# Revit family: P300328-009
name_source: partatom
category: Lighting Fixtures
revit_build: Autodesk Revit 2017 (Build: 20160225_1515(x64)
units: mm (PartAtom-declared; Revit-internal decimal feet)

## family parameters
Cut with Voids When Loaded = No
Host = Face
Light Source = No
OmniClass Number = 23.80.70.11.14.17
OmniClass Title = Direct/Indirect
Part Type = Normal
Room Calculation Point = No
Round Connector Dimension = Use Diameter
Shared = Yes

## types (1)
- P300328-009
    Apparent Load = 100 VA
    Assembly Code = D5020200
    Connector Description = Lighting Connector
    Default Elevation = 48 "
    Description = Merry Collection Two-Light Brushed Nickel and Etched Glass Transitional Style Bath Vanity Wall Light
    Features = Bring a modern vibe to any room with the Merry Collection 2-Light Brushed Nickel Etched Glass Transitional Bath Vanity Light. The clean-lined frame, tubular arm, and round light base are coated in a silver brushed nickel finish. A light source glows from inside a crisp etched glass shade.
Application: Bring a modern vibe to any room with the Merry Collection 2-Light Brushed Nickel Etched Glass Transitional Bath Vanity Light ideal for any entryway, hallway, foyer, bedroom, sitting room, living room, or bathroom.
Styles: Perfect for transitional and contemporary style settings.
Finish: The clean-lined frame, tubular arm, and round light base are coated in silver brushed nickel finish.
Materials: Constructed from steel to ensure a long product lifespan. Mount the light fixture facing up or down.
Glass/Shade: Light sources glow from inside crisp etched glass shades.
Bulbs: For ideal illumination, use 2 medium base bulbs that are sold separately (100w max - LED/CFL/incandescent). Compatible with dimmable bulbs.
Dimensions: Measures 12-inch width by 8-1/4-inch height by 5-3/4-inch depth.
Certifications: cULus damp location listed.
Pairs With: Pairs with the Tobin, Etched Glass, and Dome Glass collections.
Warranty: Our 1-Year Limited Warranty guarantees your complete satisfaction with your purchase and includes professional after-sales customer service support.
    Glass = Paint - Hubbell - White Texture
    Housing Material = Paint - Hubbell - Metallic Silver Textured
    Lamp = LED/CFL/incandescent
    Load Classification = Lighting
    Manufacturer = Progress Lighting
    Model = P300328-009
    Power Factor = 1
    Product Documentation Link = https://hubbellcdn.com
    Product Link = https://www.hubbell.com
    URL = https://www.hubbell.com
    Voltage = 120 V
    Warranty = 1 year Warranty
    Wattage Comments = 100W
    Watts = 100 W

## geometry (parser evidence)
native form markers: Sweep x4
no freeform markers — native parametric forms only
